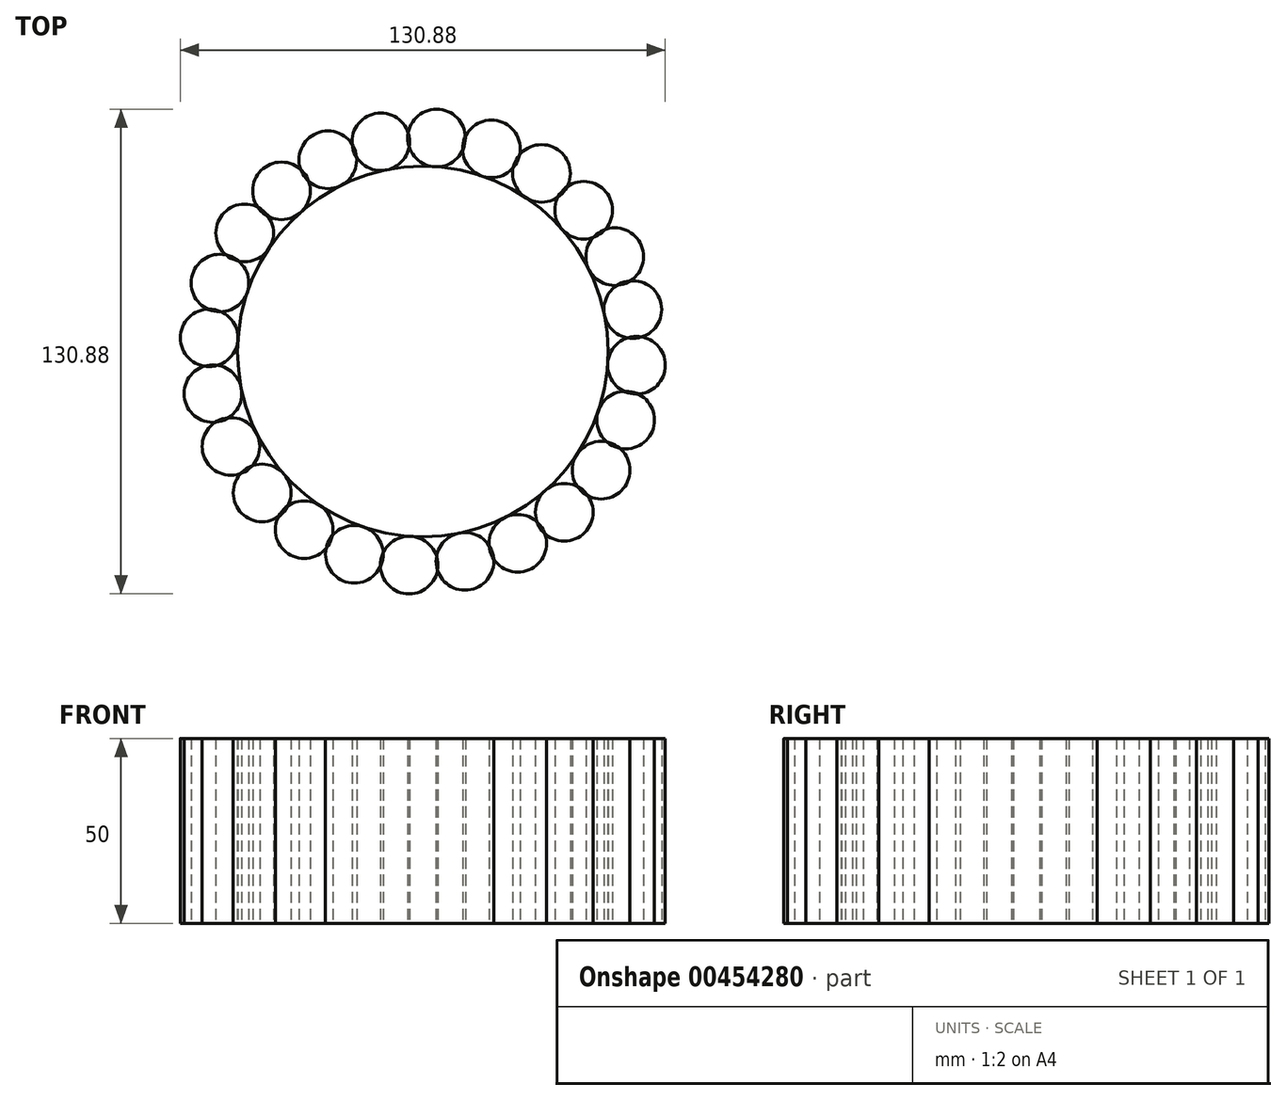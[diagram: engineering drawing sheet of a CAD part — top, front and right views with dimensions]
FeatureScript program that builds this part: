
annotation { "Feature Type Name" : "Feature", "Feature Type Description" : "" }
export const myFeature = defineFeature(function(context is Context, id is Id, definition is map)
    precondition{}
    {
        {
            var Q0;
            Q0=qCreatedBy(makeId("Top.planeOp"),FACE);
            var sketch = newSketch(context, id + "F0", { "sketchPlane" : qUnion([Q0])});
            skCircle(sketch, "E0", {"center": v(0, 0) * mm, "radius": 50 * mm});
            skSolve(sketch);
        }
        {
            var Q0;
            Q0 = qSketchRegion(id + "F0", true);
            extrude(context, id + "F1", {"entities" : qUnion([Q0]), "depth" : 50 * mm});
        }
        {
            var Q0;
            Q0=qCreatedBy(makeId("Top.planeOp"),FACE);
            var sketch = newSketch(context, id + "F2", { "sketchPlane" : qUnion([Q0])});
            skCircle(sketch, "E1", {"center": v(3.7, 57.66) * mm, "radius": 7.78 * mm});
            skSolve(sketch);
        }
        {
            var Q0;
            Q0=makeQuery(id+"F2.imprint","IMPRINT",FACE,{"disambiguationData":[TD([[makeQuery(id+"F2.imprint","IMPRINT",EDGE,{"derivedFrom":sQuery(id+"F2.wireOp",EDGE,"E1")}),1.0]])]});
            extrude(context, id + "F3", {"entities" : qUnion([Q0]), "operationType" : NewBodyOperationType.ADD, "depth" : 50 * mm});
        }
        {
            var Q0;
            Q0=makeQuery(id+"F3.opExtrude","SWEPT_BODY",BODY,{"disambiguationData":[OSD([sQuery(id+"F2.wireOp",EDGE,"E1")])]});
            var Q1;
            Q1=makeQuery(id+"F1.opExtrude","CAP_EDGE",EDGE,{"disambiguationData":[OSD([sQuery(id+"F0.wireOp",EDGE,"E0")])],"isStart":false});
            circularPattern(context, id + "F4", {"entities" : qUnion([Q0]), "axis" : qUnion([Q1]), "angle" : 360 * degree, "instanceCount" : 24, "equalSpace" : true});
        }
    });
